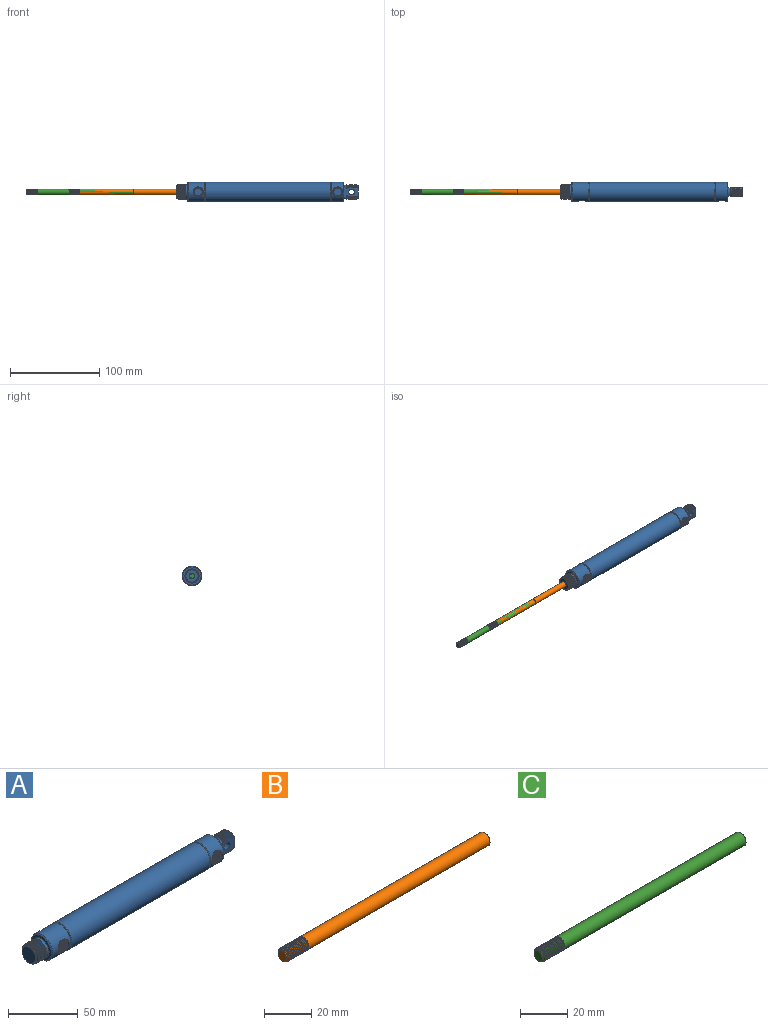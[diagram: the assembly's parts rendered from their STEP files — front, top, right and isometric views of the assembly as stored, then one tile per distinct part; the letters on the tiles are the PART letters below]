
ASSEMBLY  parts=3 mates=2
PART A: 127 faces, bbox 205.6x22.4x22.4 mm
  f0: cone r=5.14mm half-angle=45deg, axis (0,-1,0), area 13.3mm2, adj f116,f122,f123,f124
  f1: cone r=5.14mm half-angle=45deg, axis (0,-1,0), area 13.3mm2, adj f113,f117,f118,f119
  f2: cylinder r=10.92mm len=21.84mm, axis (-1,0,0), area 782mm2, adj f13,f14,f114,f115
  f3: cylinder r=10.92mm len=21.84mm, axis (-1,0,0), area 1155.5mm2, adj f8,f10,f111,f112
  f4: plane 20.32x20.32mm, normal (1,0,0), area 181.1mm2, adj f14,f32,f94,f95,f96
  f5: cylinder r=10.92mm len=140.53mm, axis (-1,0,0), area 9644mm2, adj f6,f11
  f6: cone r=10.65mm half-angle=26.6deg, axis (1,0,0), area 41.4mm2, adj f5,f7
  f7: plane 21.3x21.3mm, normal (-1,0,0), area 18mm2, adj f6,f8
  f8: cone r=10.92mm half-angle=45deg, axis (-1,0,0), area 51.7mm2, adj f3,f7
  f9: plane 20.32x20.32mm, normal (-1,0,0), area 126.4mm2, adj f10,f104
  f10: cone r=10.16mm half-angle=45deg, axis (1,0,0), area 71.4mm2, adj f3,f9
  f11: cone r=10.92mm half-angle=26.6deg, axis (-1,0,0), area 41.4mm2, adj f5,f12
  f12: plane 21.3x21.3mm, normal (1,0,0), area 18mm2, adj f11,f13
  f13: cone r=10.38mm half-angle=45deg, axis (1,0,0), area 51.7mm2, adj f2,f12
  f14: cone r=10.92mm half-angle=45deg, axis (-1,0,0), area 71.4mm2, adj f2,f4
  f15: bspline ~5.61x2.97mm, area 0mm2, adj f16,f31,f96
  f16: bspline ~9.93x2.06mm, area 0.6mm2, adj f15,f27,f31,f96
  f17: cylinder r=7.94mm len=9.65mm, axis (1,0,0), area 1.8mm2, adj f23,f25,f95,f96
  f18: bspline ~9.93x2.06mm, area 1.9mm2, adj f21,f24,f95,f96
  f19: bspline ~9.93x2.06mm, area 1.9mm2, adj f22,f25,f95,f96
  f20: bspline ~9.93x2.06mm, area 1.9mm2, adj f23,f67,f95,f96
  f21: bspline ~11.23x2.97mm, area 9.8mm2, adj f18,f62,f95,f96
  f22: bspline ~11.23x2.97mm, area 11.2mm2, adj f19,f28,f95,f96
  f23: bspline ~11.23x2.97mm, area 11.2mm2, adj f17,f20,f95,f96
  f24: bspline ~11.23x2.97mm, area 11.2mm2, adj f18,f28,f95,f96
  f25: bspline ~11.23x2.97mm, area 11.2mm2, adj f17,f19,f95,f96
  f26: cylinder r=7.94mm len=9.65mm, axis (1,0,0), area 1.8mm2, adj f27,f51,f95,f96
  f27: bspline ~11.23x2.97mm, area 9.9mm2, adj f16,f26,f31,f95,f96
  f28: cylinder r=7.94mm len=9.65mm, axis (1,0,0), area 1.8mm2, adj f22,f24,f95,f96
  f29: cone r=6.88mm half-angle=45deg, axis (-1,0,0), area 7.5mm2, adj f41,f64,f95,f96
  f30: plane 9.72x2.78mm, normal (1,0,0), area 9.2mm2, adj f47,f48,f49,f94,f95,f96
  f31: torus R=7.56mm, axis (-1,0,0), area 33.8mm2, adj f15,f16,f27,f91,f95,f96
  f32: cylinder r=7.94mm len=9.65mm, axis (1,0,0), area 23.7mm2, adj f4,f91,f95,f96
  f33: cylinder r=7.94mm len=1.02mm, axis (1,0,0), area 0mm2, adj f34,f93,f95
  f34: bspline ~11.23x2.97mm, area 8.7mm2, adj f33,f35,f92,f93,f95,f96
  f35: bspline ~9.93x2.06mm, area 1.9mm2, adj f34,f52,f95,f96
  f36: cylinder r=7.94mm len=9.65mm, axis (1,0,0), area 1.8mm2, adj f46,f70,f95,f96
  f37: cylinder r=7.94mm len=9.65mm, axis (1,0,0), area 1.8mm2, adj f43,f45,f95,f96
  f38: bspline ~9.93x2.06mm, area 1.9mm2, adj f41,f44,f95,f96
  f39: bspline ~9.93x2.06mm, area 1.9mm2, adj f42,f45,f95,f96
  f40: bspline ~9.93x2.06mm, area 1.9mm2, adj f43,f46,f95,f96
  f41: bspline ~11.23x2.97mm, area 4.4mm2, adj f29,f38,f95,f96
  f42: bspline ~11.23x2.97mm, area 11.2mm2, adj f39,f61,f95,f96
  f43: bspline ~11.23x2.97mm, area 11.2mm2, adj f37,f40,f95,f96
  f44: bspline ~11.23x2.97mm, area 11.2mm2, adj f38,f61,f95,f96
  f45: bspline ~11.23x2.97mm, area 11.2mm2, adj f37,f39,f95,f96
  f46: bspline ~11.23x2.97mm, area 11.2mm2, adj f36,f40,f95,f96
  f47: bspline ~9.93x2.06mm, area 0.6mm2, adj f30,f48,f49,f92,f95
  f48: bspline ~11.23x2.97mm, area 0.7mm2, adj f30,f47,f92,f96
  f49: bspline ~5.61x2.97mm, area 0.1mm2, adj f30,f47,f95
  f50: cylinder r=7.94mm len=9.65mm, axis (1,0,0), area 1.8mm2, adj f52,f89,f95,f96
  f51: bspline ~11.23x2.97mm, area 11.2mm2, adj f26,f53,f95,f96
  f52: bspline ~11.23x2.97mm, area 11.2mm2, adj f35,f50,f95,f96
  f53: bspline ~9.93x2.06mm, area 1.9mm2, adj f51,f90,f95,f96
  f54: cylinder r=7.94mm len=9.65mm, axis (1,0,0), area 1.8mm2, adj f67,f73,f95,f96
  f55: cylinder r=7.94mm len=9.65mm, axis (1,0,0), area 1.8mm2, adj f71,f76,f95,f96
  f56: cylinder r=7.94mm len=9.65mm, axis (1,0,0), area 1.8mm2, adj f74,f79,f95,f96
  f57: cylinder r=7.94mm len=9.65mm, axis (1,0,0), area 1.8mm2, adj f77,f82,f95,f96
  f58: cylinder r=7.94mm len=9.65mm, axis (1,0,0), area 1.8mm2, adj f80,f85,f95,f96
  f59: cylinder r=7.94mm len=9.65mm, axis (1,0,0), area 1.8mm2, adj f83,f88,f95,f96
  f60: cylinder r=7.94mm len=9.65mm, axis (1,0,0), area 1.8mm2, adj f86,f90,f95,f96
  f61: cylinder r=7.94mm len=9.65mm, axis (1,0,0), area 1.8mm2, adj f42,f44,f95,f96
  f62: cone r=6.88mm half-angle=45deg, axis (-1,0,0), area 12mm2, adj f21,f64,f65,f66,f68,f95,f96
  f63: cylinder r=3.17mm len=9.65mm, axis (0,-1,0), area 192.5mm2, adj f95,f96
  f64: plane 13.76x9.65mm, normal (1,0,0), area 120.9mm2, adj f29,f62,f95,f96
  f65: bspline ~9.93x2.06mm, area 0.7mm2, adj f62,f66,f68,f95
  f66: bspline ~5.61x2.97mm, area 0mm2, adj f62,f65,f95
  f67: bspline ~11.23x2.97mm, area 11.2mm2, adj f20,f54,f95,f96
  f68: bspline ~11.23x2.97mm, area 1.7mm2, adj f62,f65,f95
  f69: bspline ~9.93x2.06mm, area 1.9mm2, adj f70,f71,f95,f96
  f70: bspline ~11.23x2.97mm, area 11.2mm2, adj f36,f69,f95,f96
  f71: bspline ~11.23x2.97mm, area 11.2mm2, adj f55,f69,f95,f96
  f72: bspline ~9.93x2.06mm, area 1.9mm2, adj f73,f74,f95,f96
  f73: bspline ~11.23x2.97mm, area 11.2mm2, adj f54,f72,f95,f96
  f74: bspline ~11.23x2.97mm, area 11.2mm2, adj f56,f72,f95,f96
  f75: bspline ~9.93x2.06mm, area 1.9mm2, adj f76,f77,f95,f96
  f76: bspline ~11.23x2.97mm, area 11.2mm2, adj f55,f75,f95,f96
  f77: bspline ~11.23x2.97mm, area 11.2mm2, adj f57,f75,f95,f96
  f78: bspline ~9.93x2.06mm, area 1.9mm2, adj f79,f80,f95,f96
  f79: bspline ~11.23x2.97mm, area 11.2mm2, adj f56,f78,f95,f96
  f80: bspline ~11.23x2.97mm, area 11.2mm2, adj f58,f78,f95,f96
  f81: bspline ~9.93x2.06mm, area 1.9mm2, adj f82,f83,f95,f96
  f82: bspline ~11.23x2.97mm, area 11.2mm2, adj f57,f81,f95,f96
  f83: bspline ~11.23x2.97mm, area 11.2mm2, adj f59,f81,f95,f96
  f84: bspline ~9.93x2.06mm, area 1.9mm2, adj f85,f86,f95,f96
  f85: bspline ~11.23x2.97mm, area 11.2mm2, adj f58,f84,f95,f96
  f86: bspline ~11.23x2.97mm, area 11.2mm2, adj f60,f84,f95,f96
  f87: bspline ~9.93x2.06mm, area 1.9mm2, adj f88,f89,f95,f96
  f88: bspline ~11.23x2.97mm, area 11.2mm2, adj f59,f87,f95,f96
  f89: bspline ~11.23x2.97mm, area 11.2mm2, adj f50,f87,f95,f96
  f90: bspline ~11.23x2.97mm, area 11.2mm2, adj f53,f60,f95,f96
  f91: plane 9.65x2.12mm, normal (1,0,0), area 4mm2, adj f31,f32,f95,f96
  f92: torus R=7.56mm, axis (-1,0,0), area 33.6mm2, adj f34,f47,f48,f93,f95,f96
  f93: plane 8.4x2.06mm, normal (-1,0,0), area 1.9mm2, adj f33,f34,f92,f95
  f94: cylinder r=7.94mm len=9.65mm, axis (1,0,0), area 23.7mm2, adj f4,f30,f95,f96
  f95: plane 15.81x12.66mm, normal (0,-1,0), area 145.2mm2, adj f4,f17,f18,f19,f20,f21,f22,f23
  f96: plane 15.81x12.66mm, normal (0,1,0), area 144.8mm2, adj f4,f15,f16,f17,f18,f19,f20,f21
  f97: plane 16.45x16.45mm, normal (-1,0,0), area 21.9mm2, adj f104,f106,f107,f108
  f98: cylinder r=7.94mm len=15.88mm, axis (1,0,0), area 8.8mm2, adj f99,f105,f106,f108
  f99: cylinder r=7.94mm len=15.88mm, axis (1,0,0), area 8.8mm2, adj f98,f100,f106,f108
  f100: cylinder r=7.94mm len=15.88mm, axis (1,0,0), area 8.8mm2, adj f99,f101,f106,f108
  f101: cylinder r=7.94mm len=15.88mm, axis (1,0,0), area 8.8mm2, adj f100,f102,f106,f108
  f102: cylinder r=7.94mm len=15.88mm, axis (1,0,0), area 8.8mm2, adj f101,f103,f106,f108
  f103: cylinder r=7.94mm len=15.88mm, axis (1,0,0), area 8.8mm2, adj f102,f104,f106,f108
  f104: cylinder r=7.94mm len=15.88mm, axis (1,0,0), area 119mm2, adj f9,f97,f103,f106,f108
  f105: cylinder r=7.94mm len=5.61mm, axis (1,0,0), area 0.6mm2, adj f98,f108,f110
  f106: bspline ~15.88x15.88mm, area 345.7mm2, adj f97,f98,f99,f100,f101,f102,f103,f104
  f107: bspline ~14.04x14.04mm, area 56.6mm2, adj f97,f106,f108,f110
  f108: bspline ~15.88x15.88mm, area 317mm2, adj f97,f98,f99,f100,f101,f102,f103,f104
  f109: plane 13.76x13.76mm, normal (-1,0,0), area 148.7mm2, adj f110
  f110: cone r=7.94mm half-angle=45deg, axis (1,0,0), area 38.7mm2, adj f105,f106,f107,f108,f109
  f111: cylinder r=5.66mm len=11.32mm, axis (0,1,0), area 14mm2, adj f3,f113
  f112: cylinder r=5.66mm len=11.32mm, axis (0,1,0), area 14mm2, adj f3,f113
  f113: plane 11.32x11.32mm, normal (0,-1,0), area 17.5mm2, adj f1,f111,f112,f120
  f114: cylinder r=5.66mm len=11.32mm, axis (0,1,0), area 0mm2, adj f2,f116
  f115: cylinder r=5.66mm len=11.32mm, axis (0,1,0), area 0mm2, adj f2,f116
  f116: plane 11.32x11.32mm, normal (0,-1,0), area 17.5mm2, adj f0,f114,f115,f125
  f117: bspline ~10.29x10.29mm, area 126.3mm2, adj f1,f118,f120,f121
  f118: bspline ~9.07x9.07mm, area 18.6mm2, adj f1,f117,f119,f121
  f119: bspline ~10.29x10.29mm, area 126.4mm2, adj f1,f118,f120,f121
  f120: cylinder r=5.14mm len=10.29mm, axis (0,-1,0), area 23.6mm2, adj f113,f117,f119,f121
  f121: plane 10.09x10.09mm, normal (0,-1,0), area 73.7mm2, adj f117,f118,f119,f120
  f122: bspline ~10.29x10.29mm, area 126.3mm2, adj f0,f123,f125,f126
  f123: bspline ~9.07x9.07mm, area 18.6mm2, adj f0,f122,f124,f126
  f124: bspline ~10.29x10.29mm, area 126.4mm2, adj f0,f123,f125,f126
  f125: cylinder r=5.14mm len=10.29mm, axis (0,-1,0), area 23.6mm2, adj f116,f122,f124,f126
  f126: plane 10.09x10.09mm, normal (0,-1,0), area 73.7mm2, adj f122,f123,f124,f125
PART B: 21 faces, bbox 121.3x6.7x6.7 mm
  f0: cylinder r=3.17mm len=6.35mm, axis (-1,0,0), area 1.3mm2, adj f1,f15,f16,f18
  f1: cylinder r=3.17mm len=6.35mm, axis (-1,0,0), area 2.3mm2, adj f0,f2,f16,f18
  f2: cylinder r=3.17mm len=6.35mm, axis (-1,0,0), area 2.3mm2, adj f1,f3,f16,f18
  f3: cylinder r=3.17mm len=6.35mm, axis (-1,0,0), area 2.3mm2, adj f2,f4,f16,f18
  f4: cylinder r=3.17mm len=6.35mm, axis (-1,0,0), area 2.3mm2, adj f3,f5,f16,f18
  f5: cylinder r=3.17mm len=6.35mm, axis (-1,0,0), area 2.3mm2, adj f4,f6,f16,f18
  f6: cylinder r=3.17mm len=6.35mm, axis (-1,0,0), area 2.3mm2, adj f5,f7,f16,f18
  f7: cylinder r=3.17mm len=6.35mm, axis (-1,0,0), area 2.3mm2, adj f6,f8,f16,f18
  f8: cylinder r=3.17mm len=6.35mm, axis (-1,0,0), area 2.3mm2, adj f7,f9,f16,f18
  f9: cylinder r=3.17mm len=6.35mm, axis (-1,0,0), area 2.3mm2, adj f8,f10,f16,f18
  f10: cylinder r=3.17mm len=6.35mm, axis (-1,0,0), area 2.3mm2, adj f9,f11,f16,f18
  f11: cylinder r=3.17mm len=6.35mm, axis (-1,0,0), area 2.3mm2, adj f10,f12,f16,f18
  f12: cylinder r=3.17mm len=6.35mm, axis (-1,0,0), area 2.3mm2, adj f11,f13,f16,f18
  f13: cylinder r=3.17mm len=108.63mm, axis (-1,0,0), area 2155.1mm2, adj f12,f16,f18,f19,f20
  f14: plane 4.99x4.99mm, normal (-1,0,0), area 19.6mm2, adj f15
  f15: cone r=2.49mm half-angle=45deg, axis (1,0,0), area 9.4mm2, adj f0,f14,f16,f17,f18
  f16: bspline ~13.04x6.35mm, area 167.1mm2, adj f0,f1,f2,f3,f4,f5,f6,f7
  f17: bspline ~12.93x5.17mm, area 25.6mm2, adj f15,f16,f18,f19
  f18: bspline ~13.49x6.35mm, area 166.4mm2, adj f0,f1,f2,f3,f4,f5,f6,f7
  f19: plane 6.71x6.71mm, normal (-1,0,0), area 5.5mm2, adj f13,f16,f17,f18
  f20: plane 6.35x6.35mm, normal (1,0,0), area 31.7mm2, adj f13
PART C: 21 faces, bbox 121.3x6.7x6.7 mm
  f0: cylinder r=3.17mm len=6.35mm, axis (-1,0,0), area 1.3mm2, adj f1,f15,f16,f18
  f1: cylinder r=3.17mm len=6.35mm, axis (-1,0,0), area 2.3mm2, adj f0,f2,f16,f18
  f2: cylinder r=3.17mm len=6.35mm, axis (-1,0,0), area 2.3mm2, adj f1,f3,f16,f18
  f3: cylinder r=3.17mm len=6.35mm, axis (-1,0,0), area 2.3mm2, adj f2,f4,f16,f18
  f4: cylinder r=3.17mm len=6.35mm, axis (-1,0,0), area 2.3mm2, adj f3,f5,f16,f18
  f5: cylinder r=3.17mm len=6.35mm, axis (-1,0,0), area 2.3mm2, adj f4,f6,f16,f18
  f6: cylinder r=3.17mm len=6.35mm, axis (-1,0,0), area 2.3mm2, adj f5,f7,f16,f18
  f7: cylinder r=3.17mm len=6.35mm, axis (-1,0,0), area 2.3mm2, adj f6,f8,f16,f18
  f8: cylinder r=3.17mm len=6.35mm, axis (-1,0,0), area 2.3mm2, adj f7,f9,f16,f18
  f9: cylinder r=3.17mm len=6.35mm, axis (-1,0,0), area 2.3mm2, adj f8,f10,f16,f18
  f10: cylinder r=3.17mm len=6.35mm, axis (-1,0,0), area 2.3mm2, adj f9,f11,f16,f18
  f11: cylinder r=3.17mm len=6.35mm, axis (-1,0,0), area 2.3mm2, adj f10,f12,f16,f18
  f12: cylinder r=3.17mm len=6.35mm, axis (-1,0,0), area 2.3mm2, adj f11,f13,f16,f18
  f13: cylinder r=3.17mm len=108.63mm, axis (-1,0,0), area 2155.1mm2, adj f12,f16,f18,f19,f20
  f14: plane 4.99x4.99mm, normal (-1,0,0), area 19.6mm2, adj f15
  f15: cone r=2.49mm half-angle=45deg, axis (1,0,0), area 9.4mm2, adj f0,f14,f16,f17,f18
  f16: bspline ~13.04x6.35mm, area 167.1mm2, adj f0,f1,f2,f3,f4,f5,f6,f7
  f17: bspline ~12.93x5.17mm, area 25.6mm2, adj f15,f16,f18,f19
  f18: bspline ~13.49x6.35mm, area 166.4mm2, adj f0,f1,f2,f3,f4,f5,f6,f7
  f19: plane 6.71x6.71mm, normal (-1,0,0), area 5.5mm2, adj f13,f16,f17,f18
  f20: plane 6.35x6.35mm, normal (1,0,0), area 31.7mm2, adj f13
PLACE A t=(-10.5,26.15,-30.71)mm fixed
PLACE B t=(-118.45,26.15,-30.71)mm
PLACE C t=(-64.7,26.15,-30.71)mm
MATE slider A.f6 <-> B.f0  axis (-1,0,0) through (-106.13,26.15,-30.71)mm
MATE slider C.f0 <-> B.f0  axis (-1,0,0) through (-153.98,26.15,-30.71)mm
